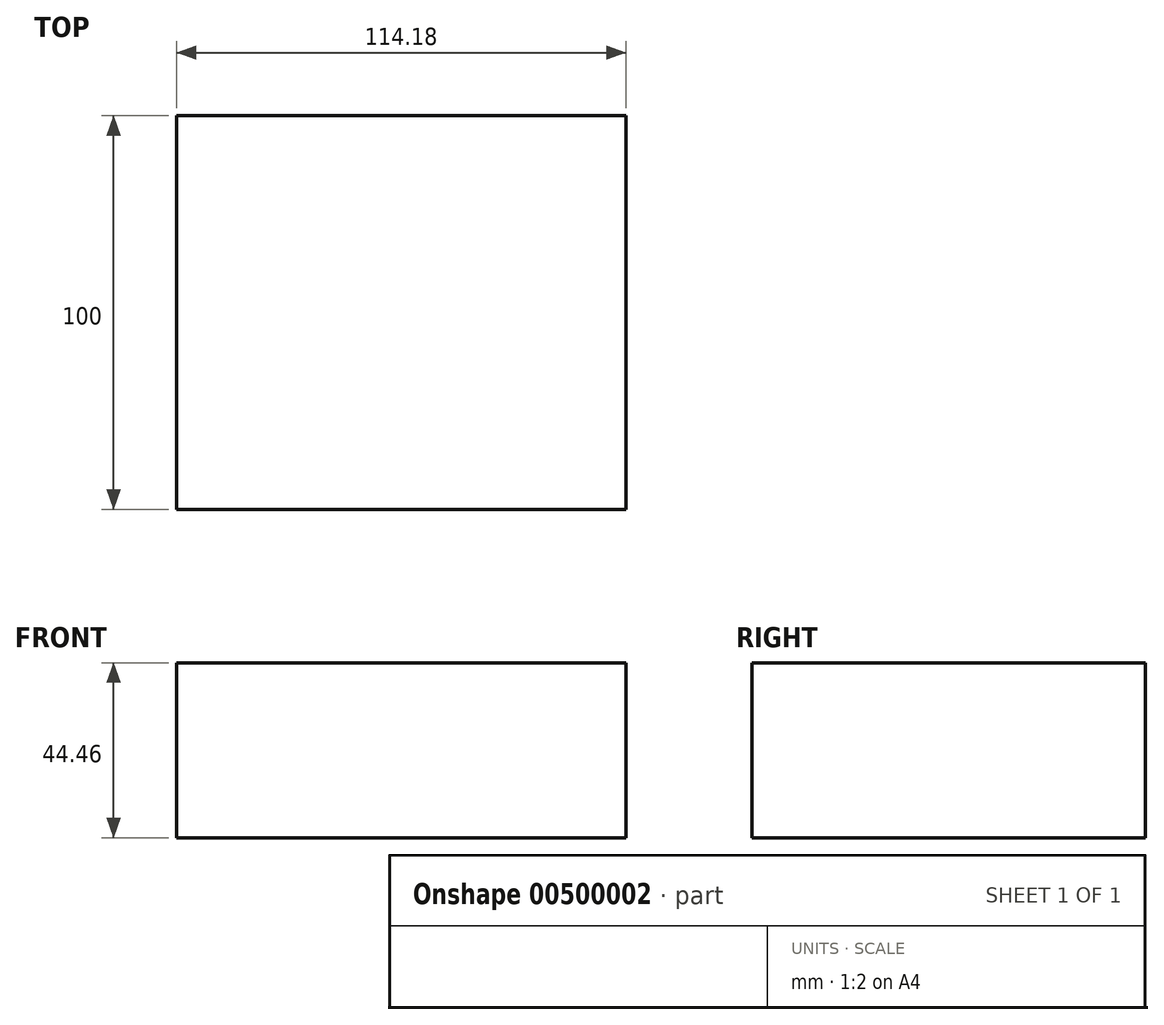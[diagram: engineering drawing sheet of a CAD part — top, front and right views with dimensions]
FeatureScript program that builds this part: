
annotation { "Feature Type Name" : "Feature", "Feature Type Description" : "" }
export const myFeature = defineFeature(function(context is Context, id is Id, definition is map)
    precondition{}
    {
        {
            var Q0;
            Q0=qCreatedBy(makeId("Front.planeOp"),FACE);
            var sketch = newSketch(context, id + "F0", { "sketchPlane" : qUnion([Q0])});
            skLineSegment(sketch, "E0.bottom", {"start": v(-57.1, 22.23) * mm, "end": v(57.1, 22.23) * mm});
            skLineSegment(sketch, "E0.top", {"start": v(-57.1, -22.23) * mm, "end": v(57.1, -22.23) * mm});
            skLineSegment(sketch, "E0.left", {"start": v(-57.1, 22.23) * mm, "end": v(-57.1, -22.23) * mm});
            skLineSegment(sketch, "E0.right", {"start": v(57.1, 22.23) * mm, "end": v(57.1, -22.23) * mm});
            skPoint(sketch, "E0.middle", {"position": v(0, 0) * mm});
            skSolve(sketch);
        }
        {
            var Q0;
            Q0 = qSketchRegion(id + "F0", true);
            extrude(context, id + "F1", {"entities" : qUnion([Q0]), "endBound" : BoundingType.SYMMETRIC, "depth" : 100 * mm});
        }
    });
